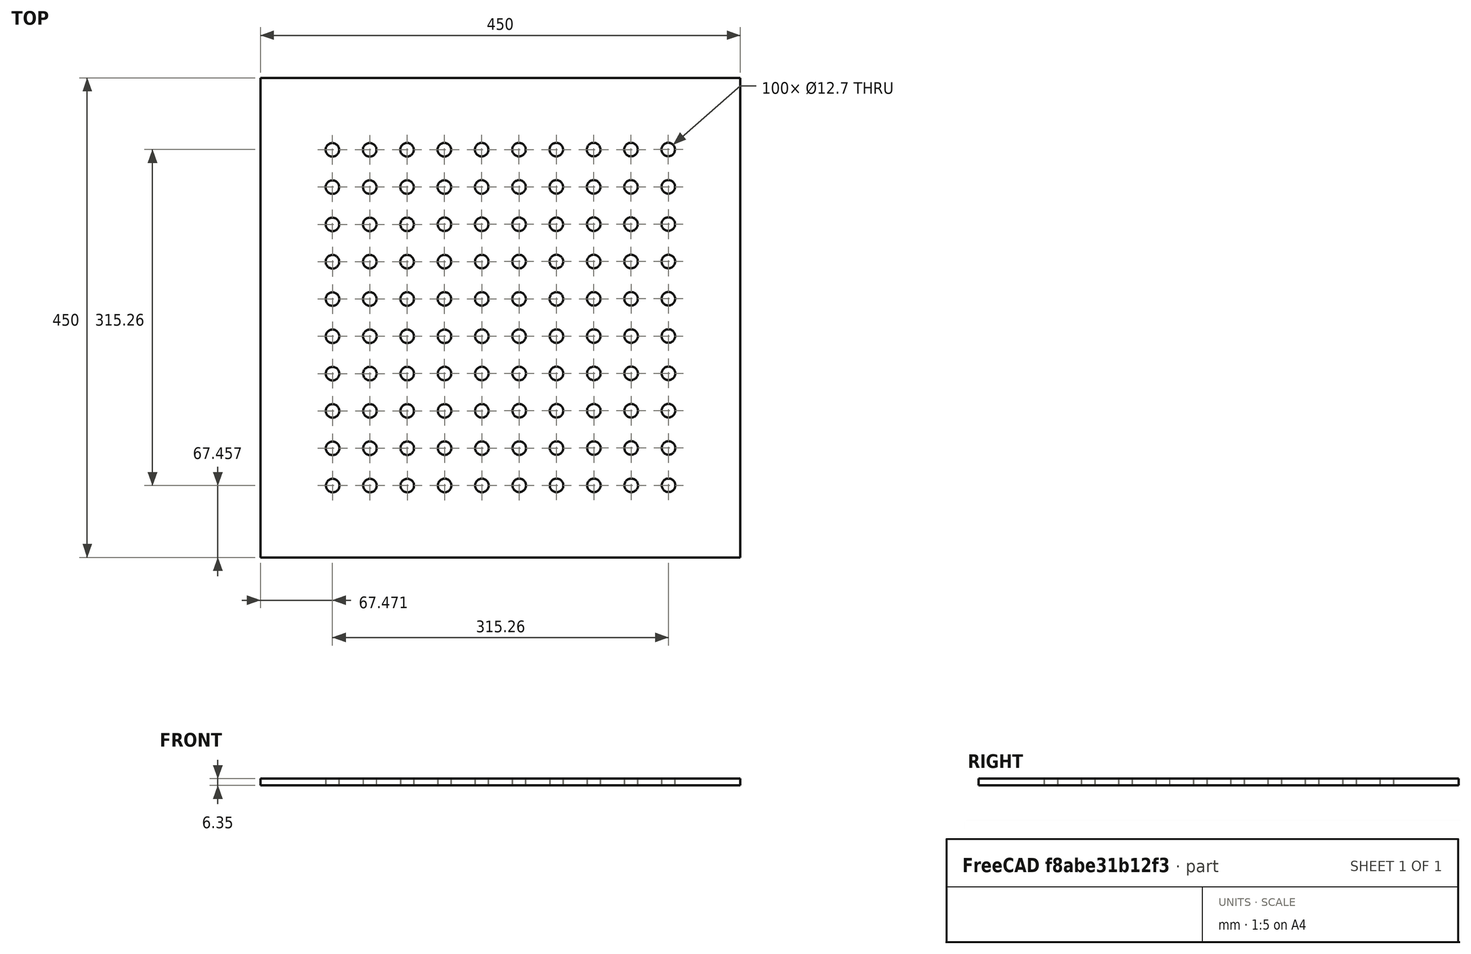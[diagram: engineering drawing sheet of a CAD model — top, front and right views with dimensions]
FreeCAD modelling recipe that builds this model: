
FCSTD DOCUMENT  (FreeCAD 0.16RUnknown)
Label: Tapa Perforada
License: All rights reserved
LicenseURL: http://berserk.design
objects: Sketcher::SketchObject×1, PartDesign::Pad×1
note: 3 computed .brp shape members not serialized (recipe doc carries the construction recipe); baked Part::Feature solids carry a one-line shape summary decoded from their .brp

FEATURE [Sketcher::SketchObject] Sketch
  sketch-geometry (207):
    g0: LineSegment StartX=0 StartY=0 StartZ=0 EndX=450 EndY=0 EndZ=0
    g1: LineSegment StartX=450 StartY=0 StartZ=0 EndX=450 EndY=450 EndZ=0
    g2: LineSegment StartX=450 StartY=450 StartZ=0 EndX=0 EndY=450 EndZ=0
    g3: LineSegment StartX=0 StartY=450 StartZ=0 EndX=0 EndY=0 EndZ=0
    g4: Circle CenterX=67.4711 CenterY=382.457 CenterZ=0 NormalX=0 NormalY=0 NormalZ=1 Radius=6.35
    g5: Circle CenterX=102.471 CenterY=382.485 CenterZ=0 NormalX=0 NormalY=0 NormalZ=1 Radius=6.35
    g6: LineSegment [constr] StartX=67.4711 StartY=382.457 StartZ=0 EndX=102.471 EndY=382.485 EndZ=0
    g7: Circle CenterX=137.471 CenterY=382.514 CenterZ=0 NormalX=0 NormalY=0 NormalZ=1 Radius=6.35
    g8: LineSegment [constr] StartX=102.471 StartY=382.485 StartZ=0 EndX=137.471 EndY=382.514 EndZ=0
    g9: Circle CenterX=172.471 CenterY=382.543 CenterZ=0 NormalX=0 NormalY=0 NormalZ=1 Radius=6.35
    g10: LineSegment [constr] StartX=137.471 StartY=382.514 StartZ=0 EndX=172.471 EndY=382.543 EndZ=0
    g11: Circle CenterX=207.471 CenterY=382.572 CenterZ=0 NormalX=0 NormalY=0 NormalZ=1 Radius=6.35
    g12: LineSegment [constr] StartX=172.471 StartY=382.543 StartZ=0 EndX=207.471 EndY=382.572 EndZ=0
    g13: Circle CenterX=242.471 CenterY=382.601 CenterZ=0 NormalX=0 NormalY=0 NormalZ=1 Radius=6.35
    g14: LineSegment [constr] StartX=207.471 StartY=382.572 StartZ=0 EndX=242.471 EndY=382.601 EndZ=0
    g15: Circle CenterX=277.471 CenterY=382.63 CenterZ=0 NormalX=0 NormalY=0 NormalZ=1 Radius=6.35
    g16: LineSegment [constr] StartX=242.471 StartY=382.601 StartZ=0 EndX=277.471 EndY=382.63 EndZ=0
    g17: Circle CenterX=312.471 CenterY=382.659 CenterZ=0 NormalX=0 NormalY=0 NormalZ=1 Radius=6.35
    g18: LineSegment [constr] StartX=277.471 StartY=382.63 StartZ=0 EndX=312.471 EndY=382.659 EndZ=0
    g19: Circle CenterX=347.471 CenterY=382.688 CenterZ=0 NormalX=0 NormalY=0 NormalZ=1 Radius=6.35
    g20: LineSegment [constr] StartX=312.471 StartY=382.659 StartZ=0 EndX=347.471 EndY=382.688 EndZ=0
    g21: Circle CenterX=382.471 CenterY=382.717 CenterZ=0 NormalX=0 NormalY=0 NormalZ=1 Radius=6.35
    g22: LineSegment [constr] StartX=347.471 StartY=382.688 StartZ=0 EndX=382.471 EndY=382.717 EndZ=0
    g23: Circle CenterX=67.5001 CenterY=347.457 CenterZ=0 NormalX=0 NormalY=0 NormalZ=1 Radius=6.35
    g24: LineSegment [constr] StartX=67.4711 StartY=382.457 StartZ=0 EndX=67.5001 EndY=347.457 EndZ=0
    g25: Circle CenterX=102.5 CenterY=347.485 CenterZ=0 NormalX=0 NormalY=0 NormalZ=1 Radius=6.35
    g26: LineSegment [constr] StartX=67.5001 StartY=347.457 StartZ=0 EndX=102.5 EndY=347.485 EndZ=0
    g27: Circle CenterX=137.5 CenterY=347.514 CenterZ=0 NormalX=0 NormalY=0 NormalZ=1 Radius=6.35
    g28: LineSegment [constr] StartX=102.5 StartY=347.485 StartZ=0 EndX=137.5 EndY=347.514 EndZ=0
    g29: Circle CenterX=172.5 CenterY=347.543 CenterZ=0 NormalX=0 NormalY=0 NormalZ=1 Radius=6.35
    g30: LineSegment [constr] StartX=137.5 StartY=347.514 StartZ=0 EndX=172.5 EndY=347.543 EndZ=0
    g31: Circle CenterX=207.5 CenterY=347.572 CenterZ=0 NormalX=0 NormalY=0 NormalZ=1 Radius=6.35
    g32: LineSegment [constr] StartX=172.5 StartY=347.543 StartZ=0 EndX=207.5 EndY=347.572 EndZ=0
    g33: Circle CenterX=242.5 CenterY=347.601 CenterZ=0 NormalX=0 NormalY=0 NormalZ=1 Radius=6.35
    g34: LineSegment [constr] StartX=207.5 StartY=347.572 StartZ=0 EndX=242.5 EndY=347.601 EndZ=0
    g35: Circle CenterX=277.5 CenterY=347.63 CenterZ=0 NormalX=0 NormalY=0 NormalZ=1 Radius=6.35
    g36: LineSegment [constr] StartX=242.5 StartY=347.601 StartZ=0 EndX=277.5 EndY=347.63 EndZ=0
    g37: Circle CenterX=312.5 CenterY=347.659 CenterZ=0 NormalX=0 NormalY=0 NormalZ=1 Radius=6.35
    g38: LineSegment [constr] StartX=277.5 StartY=347.63 StartZ=0 EndX=312.5 EndY=347.659 EndZ=0
    g39: Circle CenterX=347.5 CenterY=347.688 CenterZ=0 NormalX=0 NormalY=0 NormalZ=1 Radius=6.35
    g40: LineSegment [constr] StartX=312.5 StartY=347.659 StartZ=0 EndX=347.5 EndY=347.688 EndZ=0
    g41: Circle CenterX=382.5 CenterY=347.717 CenterZ=0 NormalX=0 NormalY=0 NormalZ=1 Radius=6.35
    g42: LineSegment [constr] StartX=347.5 StartY=347.688 StartZ=0 EndX=382.5 EndY=347.717 EndZ=0
    g43: Circle CenterX=67.529 CenterY=312.457 CenterZ=0 NormalX=0 NormalY=0 NormalZ=1 Radius=6.35
    g44: LineSegment [constr] StartX=67.5001 StartY=347.457 StartZ=0 EndX=67.529 EndY=312.457 EndZ=0
    g45: Circle CenterX=102.529 CenterY=312.486 CenterZ=0 NormalX=0 NormalY=0 NormalZ=1 Radius=6.35
    g46: LineSegment [constr] StartX=67.529 StartY=312.457 StartZ=0 EndX=102.529 EndY=312.486 EndZ=0
    g47: Circle CenterX=137.529 CenterY=312.514 CenterZ=0 NormalX=0 NormalY=0 NormalZ=1 Radius=6.35
    g48: LineSegment [constr] StartX=102.529 StartY=312.486 StartZ=0 EndX=137.529 EndY=312.514 EndZ=0
    g49: Circle CenterX=172.529 CenterY=312.543 CenterZ=0 NormalX=0 NormalY=0 NormalZ=1 Radius=6.35
    g50: LineSegment [constr] StartX=137.529 StartY=312.514 StartZ=0 EndX=172.529 EndY=312.543 EndZ=0
    g51: Circle CenterX=207.529 CenterY=312.572 CenterZ=0 NormalX=0 NormalY=0 NormalZ=1 Radius=6.35
    g52: LineSegment [constr] StartX=172.529 StartY=312.543 StartZ=0 EndX=207.529 EndY=312.572 EndZ=0
    g53: Circle CenterX=242.529 CenterY=312.601 CenterZ=0 NormalX=0 NormalY=0 NormalZ=1 Radius=6.35
    g54: LineSegment [constr] StartX=207.529 StartY=312.572 StartZ=0 EndX=242.529 EndY=312.601 EndZ=0
    g55: Circle CenterX=277.529 CenterY=312.63 CenterZ=0 NormalX=0 NormalY=0 NormalZ=1 Radius=6.35
    g56: LineSegment [constr] StartX=242.529 StartY=312.601 StartZ=0 EndX=277.529 EndY=312.63 EndZ=0
    g57: Circle CenterX=312.529 CenterY=312.659 CenterZ=0 NormalX=0 NormalY=0 NormalZ=1 Radius=6.35
    g58: LineSegment [constr] StartX=277.529 StartY=312.63 StartZ=0 EndX=312.529 EndY=312.659 EndZ=0
    g59: Circle CenterX=347.529 CenterY=312.688 CenterZ=0 NormalX=0 NormalY=0 NormalZ=1 Radius=6.35
    g60: LineSegment [constr] StartX=312.529 StartY=312.659 StartZ=0 EndX=347.529 EndY=312.688 EndZ=0
    g61: Circle CenterX=382.529 CenterY=312.717 CenterZ=0 NormalX=0 NormalY=0 NormalZ=1 Radius=6.35
    g62: LineSegment [constr] StartX=347.529 StartY=312.688 StartZ=0 EndX=382.529 EndY=312.717 EndZ=0
    g63: Circle CenterX=67.5579 CenterY=277.457 CenterZ=0 NormalX=0 NormalY=0 NormalZ=1 Radius=6.35
    g64: LineSegment [constr] StartX=67.529 StartY=312.457 StartZ=0 EndX=67.5579 EndY=277.457 EndZ=0
    g65: Circle CenterX=102.558 CenterY=277.486 CenterZ=0 NormalX=0 NormalY=0 NormalZ=1 Radius=6.35
    g66: LineSegment [constr] StartX=67.5579 StartY=277.457 StartZ=0 EndX=102.558 EndY=277.486 EndZ=0
    g67: Circle CenterX=137.558 CenterY=277.514 CenterZ=0 NormalX=0 NormalY=0 NormalZ=1 Radius=6.35
    g68: LineSegment [constr] StartX=102.558 StartY=277.486 StartZ=0 EndX=137.558 EndY=277.514 EndZ=0
    g69: Circle CenterX=172.558 CenterY=277.543 CenterZ=0 NormalX=0 NormalY=0 NormalZ=1 Radius=6.35
    g70: LineSegment [constr] StartX=137.558 StartY=277.514 StartZ=0 EndX=172.558 EndY=277.543 EndZ=0
    g71: Circle CenterX=207.558 CenterY=277.572 CenterZ=0 NormalX=0 NormalY=0 NormalZ=1 Radius=6.35
    g72: LineSegment [constr] StartX=172.558 StartY=277.543 StartZ=0 EndX=207.558 EndY=277.572 EndZ=0
    g73: Circle CenterX=242.558 CenterY=277.601 CenterZ=0 NormalX=0 NormalY=0 NormalZ=1 Radius=6.35
    g74: LineSegment [constr] StartX=207.558 StartY=277.572 StartZ=0 EndX=242.558 EndY=277.601 EndZ=0
    g75: Circle CenterX=277.558 CenterY=277.63 CenterZ=0 NormalX=0 NormalY=0 NormalZ=1 Radius=6.35
    g76: LineSegment [constr] StartX=242.558 StartY=277.601 StartZ=0 EndX=277.558 EndY=277.63 EndZ=0
    g77: Circle CenterX=312.558 CenterY=277.659 CenterZ=0 NormalX=0 NormalY=0 NormalZ=1 Radius=6.35
    g78: LineSegment [constr] StartX=277.558 StartY=277.63 StartZ=0 EndX=312.558 EndY=277.659 EndZ=0
    g79: Circle CenterX=347.558 CenterY=277.688 CenterZ=0 NormalX=0 NormalY=0 NormalZ=1 Radius=6.35
    g80: LineSegment [constr] StartX=312.558 StartY=277.659 StartZ=0 EndX=347.558 EndY=277.688 EndZ=0
    g81: Circle CenterX=382.558 CenterY=277.717 CenterZ=0 NormalX=0 NormalY=0 NormalZ=1 Radius=6.35
    g82: LineSegment [constr] StartX=347.558 StartY=277.688 StartZ=0 EndX=382.558 EndY=277.717 EndZ=0
    g83: Circle CenterX=67.5868 CenterY=242.457 CenterZ=0 NormalX=0 NormalY=0 NormalZ=1 Radius=6.35
    g84: LineSegment [constr] StartX=67.5579 StartY=277.457 StartZ=0 EndX=67.5868 EndY=242.457 EndZ=0
    g85: Circle CenterX=102.587 CenterY=242.486 CenterZ=0 NormalX=0 NormalY=0 NormalZ=1 Radius=6.35
    g86: LineSegment [constr] StartX=67.5868 StartY=242.457 StartZ=0 EndX=102.587 EndY=242.486 EndZ=0
    g87: Circle CenterX=137.587 CenterY=242.514 CenterZ=0 NormalX=0 NormalY=0 NormalZ=1 Radius=6.35
    g88: LineSegment [constr] StartX=102.587 StartY=242.486 StartZ=0 EndX=137.587 EndY=242.514 EndZ=0
    g89: Circle CenterX=172.587 CenterY=242.543 CenterZ=0 NormalX=0 NormalY=0 NormalZ=1 Radius=6.35
    g90: LineSegment [constr] StartX=137.587 StartY=242.514 StartZ=0 EndX=172.587 EndY=242.543 EndZ=0
    g91: Circle CenterX=207.587 CenterY=242.572 CenterZ=0 NormalX=0 NormalY=0 NormalZ=1 Radius=6.35
    g92: LineSegment [constr] StartX=172.587 StartY=242.543 StartZ=0 EndX=207.587 EndY=242.572 EndZ=0
    g93: Circle CenterX=242.587 CenterY=242.601 CenterZ=0 NormalX=0 NormalY=0 NormalZ=1 Radius=6.35
    g94: LineSegment [constr] StartX=207.587 StartY=242.572 StartZ=0 EndX=242.587 EndY=242.601 EndZ=0
    g95: Circle CenterX=277.587 CenterY=242.63 CenterZ=0 NormalX=0 NormalY=0 NormalZ=1 Radius=6.35
    g96: LineSegment [constr] StartX=242.587 StartY=242.601 StartZ=0 EndX=277.587 EndY=242.63 EndZ=0
    g97: Circle CenterX=312.587 CenterY=242.659 CenterZ=0 NormalX=0 NormalY=0 NormalZ=1 Radius=6.35
    g98: LineSegment [constr] StartX=277.587 StartY=242.63 StartZ=0 EndX=312.587 EndY=242.659 EndZ=0
    g99: Circle CenterX=347.587 CenterY=242.688 CenterZ=0 NormalX=0 NormalY=0 NormalZ=1 Radius=6.35
    g100: LineSegment [constr] StartX=312.587 StartY=242.659 StartZ=0 EndX=347.587 EndY=242.688 EndZ=0
    g101: Circle CenterX=382.587 CenterY=242.717 CenterZ=0 NormalX=0 NormalY=0 NormalZ=1 Radius=6.35
    g102: LineSegment [constr] StartX=347.587 StartY=242.688 StartZ=0 EndX=382.587 EndY=242.717 EndZ=0
    g103: Circle CenterX=67.6157 CenterY=207.457 CenterZ=0 NormalX=0 NormalY=0 NormalZ=1 Radius=6.35
    g104: LineSegment [constr] StartX=67.5868 StartY=242.457 StartZ=0 EndX=67.6157 EndY=207.457 EndZ=0
    g105: Circle CenterX=102.616 CenterY=207.486 CenterZ=0 NormalX=0 NormalY=0 NormalZ=1 Radius=6.35
    g106: LineSegment [constr] StartX=67.6157 StartY=207.457 StartZ=0 EndX=102.616 EndY=207.486 EndZ=0
    g107: Circle CenterX=137.616 CenterY=207.514 CenterZ=0 NormalX=0 NormalY=0 NormalZ=1 Radius=6.35
    g108: LineSegment [constr] StartX=102.616 StartY=207.486 StartZ=0 EndX=137.616 EndY=207.514 EndZ=0
    g109: Circle CenterX=172.616 CenterY=207.543 CenterZ=0 NormalX=0 NormalY=0 NormalZ=1 Radius=6.35
    g110: LineSegment [constr] StartX=137.616 StartY=207.514 StartZ=0 EndX=172.616 EndY=207.543 EndZ=0
    g111: Circle CenterX=207.616 CenterY=207.572 CenterZ=0 NormalX=0 NormalY=0 NormalZ=1 Radius=6.35
    g112: LineSegment [constr] StartX=172.616 StartY=207.543 StartZ=0 EndX=207.616 EndY=207.572 EndZ=0
    g113: Circle CenterX=242.616 CenterY=207.601 CenterZ=0 NormalX=0 NormalY=0 NormalZ=1 Radius=6.35
    g114: LineSegment [constr] StartX=207.616 StartY=207.572 StartZ=0 EndX=242.616 EndY=207.601 EndZ=0
    g115: Circle CenterX=277.616 CenterY=207.63 CenterZ=0 NormalX=0 NormalY=0 NormalZ=1 Radius=6.35
    g116: LineSegment [constr] StartX=242.616 StartY=207.601 StartZ=0 EndX=277.616 EndY=207.63 EndZ=0
    g117: Circle CenterX=312.616 CenterY=207.659 CenterZ=0 NormalX=0 NormalY=0 NormalZ=1 Radius=6.35
    g118: LineSegment [constr] StartX=277.616 StartY=207.63 StartZ=0 EndX=312.616 EndY=207.659 EndZ=0
    g119: Circle CenterX=347.616 CenterY=207.688 CenterZ=0 NormalX=0 NormalY=0 NormalZ=1 Radius=6.35
    g120: LineSegment [constr] StartX=312.616 StartY=207.659 StartZ=0 EndX=347.616 EndY=207.688 EndZ=0
    g121: Circle CenterX=382.616 CenterY=207.717 CenterZ=0 NormalX=0 NormalY=0 NormalZ=1 Radius=6.35
    g122: LineSegment [constr] StartX=347.616 StartY=207.688 StartZ=0 EndX=382.616 EndY=207.717 EndZ=0
    g123: Circle CenterX=67.6447 CenterY=172.457 CenterZ=0 NormalX=0 NormalY=0 NormalZ=1 Radius=6.35
    g124: LineSegment [constr] StartX=67.6157 StartY=207.457 StartZ=0 EndX=67.6447 EndY=172.457 EndZ=0
    g125: Circle CenterX=102.645 CenterY=172.486 CenterZ=0 NormalX=0 NormalY=0 NormalZ=1 Radius=6.35
    g126: LineSegment [constr] StartX=67.6447 StartY=172.457 StartZ=0 EndX=102.645 EndY=172.486 EndZ=0
    g127: Circle CenterX=137.645 CenterY=172.514 CenterZ=0 NormalX=0 NormalY=0 NormalZ=1 Radius=6.35
    g128: LineSegment [constr] StartX=102.645 StartY=172.486 StartZ=0 EndX=137.645 EndY=172.514 EndZ=0
    g129: Circle CenterX=172.645 CenterY=172.543 CenterZ=0 NormalX=0 NormalY=0 NormalZ=1 Radius=6.35
    g130: LineSegment [constr] StartX=137.645 StartY=172.514 StartZ=0 EndX=172.645 EndY=172.543 EndZ=0
    g131: Circle CenterX=207.645 CenterY=172.572 CenterZ=0 NormalX=0 NormalY=0 NormalZ=1 Radius=6.35
    g132: LineSegment [constr] StartX=172.645 StartY=172.543 StartZ=0 EndX=207.645 EndY=172.572 EndZ=0
    g133: Circle CenterX=242.645 CenterY=172.601 CenterZ=0 NormalX=0 NormalY=0 NormalZ=1 Radius=6.35
    g134: LineSegment [constr] StartX=207.645 StartY=172.572 StartZ=0 EndX=242.645 EndY=172.601 EndZ=0
    g135: Circle CenterX=277.645 CenterY=172.63 CenterZ=0 NormalX=0 NormalY=0 NormalZ=1 Radius=6.35
    g136: LineSegment [constr] StartX=242.645 StartY=172.601 StartZ=0 EndX=277.645 EndY=172.63 EndZ=0
    g137: Circle CenterX=312.645 CenterY=172.659 CenterZ=0 NormalX=0 NormalY=0 NormalZ=1 Radius=6.35
    g138: LineSegment [constr] StartX=277.645 StartY=172.63 StartZ=0 EndX=312.645 EndY=172.659 EndZ=0
    g139: Circle CenterX=347.645 CenterY=172.688 CenterZ=0 NormalX=0 NormalY=0 NormalZ=1 Radius=6.35
    g140: LineSegment [constr] StartX=312.645 StartY=172.659 StartZ=0 EndX=347.645 EndY=172.688 EndZ=0
    g141: Circle CenterX=382.645 CenterY=172.717 CenterZ=0 NormalX=0 NormalY=0 NormalZ=1 Radius=6.35
    g142: LineSegment [constr] StartX=347.645 StartY=172.688 StartZ=0 EndX=382.645 EndY=172.717 EndZ=0
    g143: Circle CenterX=67.6736 CenterY=137.457 CenterZ=0 NormalX=0 NormalY=0 NormalZ=1 Radius=6.35
    g144: LineSegment [constr] StartX=67.6447 StartY=172.457 StartZ=0 EndX=67.6736 EndY=137.457 EndZ=0
    g145: Circle CenterX=102.674 CenterY=137.486 CenterZ=0 NormalX=0 NormalY=0 NormalZ=1 Radius=6.35
    g146: LineSegment [constr] StartX=67.6736 StartY=137.457 StartZ=0 EndX=102.674 EndY=137.486 EndZ=0
    g147: Circle CenterX=137.674 CenterY=137.514 CenterZ=0 NormalX=0 NormalY=0 NormalZ=1 Radius=6.35
    g148: LineSegment [constr] StartX=102.674 StartY=137.486 StartZ=0 EndX=137.674 EndY=137.514 EndZ=0
    g149: Circle CenterX=172.674 CenterY=137.543 CenterZ=0 NormalX=0 NormalY=0 NormalZ=1 Radius=6.35
    g150: LineSegment [constr] StartX=137.674 StartY=137.514 StartZ=0 EndX=172.674 EndY=137.543 EndZ=0
    g151: Circle CenterX=207.674 CenterY=137.572 CenterZ=0 NormalX=0 NormalY=0 NormalZ=1 Radius=6.35
    g152: LineSegment [constr] StartX=172.674 StartY=137.543 StartZ=0 EndX=207.674 EndY=137.572 EndZ=0
    g153: Circle CenterX=242.674 CenterY=137.601 CenterZ=0 NormalX=0 NormalY=0 NormalZ=1 Radius=6.35
    g154: LineSegment [constr] StartX=207.674 StartY=137.572 StartZ=0 EndX=242.674 EndY=137.601 EndZ=0
    g155: Circle CenterX=277.674 CenterY=137.63 CenterZ=0 NormalX=0 NormalY=0 NormalZ=1 Radius=6.35
    g156: LineSegment [constr] StartX=242.674 StartY=137.601 StartZ=0 EndX=277.674 EndY=137.63 EndZ=0
    g157: Circle CenterX=312.673 CenterY=137.659 CenterZ=0 NormalX=0 NormalY=0 NormalZ=1 Radius=6.35
    g158: LineSegment [constr] StartX=277.674 StartY=137.63 StartZ=0 EndX=312.673 EndY=137.659 EndZ=0
    g159: Circle CenterX=347.673 CenterY=137.688 CenterZ=0 NormalX=0 NormalY=0 NormalZ=1 Radius=6.35
    g160: LineSegment [constr] StartX=312.673 StartY=137.659 StartZ=0 EndX=347.673 EndY=137.688 EndZ=0
    g161: Circle CenterX=382.673 CenterY=137.717 CenterZ=0 NormalX=0 NormalY=0 NormalZ=1 Radius=6.35
    g162: LineSegment [constr] StartX=347.673 StartY=137.688 StartZ=0 EndX=382.673 EndY=137.717 EndZ=0
    g163: Circle CenterX=67.7025 CenterY=102.457 CenterZ=0 NormalX=0 NormalY=0 NormalZ=1 Radius=6.35
    g164: LineSegment [constr] StartX=67.6736 StartY=137.457 StartZ=0 EndX=67.7025 EndY=102.457 EndZ=0
    g165: Circle CenterX=102.702 CenterY=102.486 CenterZ=0 NormalX=0 NormalY=0 NormalZ=1 Radius=6.35
    g166: LineSegment [constr] StartX=67.7025 StartY=102.457 StartZ=0 EndX=102.702 EndY=102.486 EndZ=0
    g167: Circle CenterX=137.702 CenterY=102.515 CenterZ=0 NormalX=0 NormalY=0 NormalZ=1 Radius=6.35
    g168: LineSegment [constr] StartX=102.702 StartY=102.486 StartZ=0 EndX=137.702 EndY=102.515 EndZ=0
    g169: Circle CenterX=172.702 CenterY=102.543 CenterZ=0 NormalX=0 NormalY=0 NormalZ=1 Radius=6.35
    g170: LineSegment [constr] StartX=137.702 StartY=102.515 StartZ=0 EndX=172.702 EndY=102.543 EndZ=0
    g171: Circle CenterX=207.702 CenterY=102.572 CenterZ=0 NormalX=0 NormalY=0 NormalZ=1 Radius=6.35
    g172: LineSegment [constr] StartX=172.702 StartY=102.543 StartZ=0 EndX=207.702 EndY=102.572 EndZ=0
    g173: Circle CenterX=242.702 CenterY=102.601 CenterZ=0 NormalX=0 NormalY=0 NormalZ=1 Radius=6.35
    g174: LineSegment [constr] StartX=207.702 StartY=102.572 StartZ=0 EndX=242.702 EndY=102.601 EndZ=0
    g175: Circle CenterX=277.702 CenterY=102.63 CenterZ=0 NormalX=0 NormalY=0 NormalZ=1 Radius=6.35
    g176: LineSegment [constr] StartX=242.702 StartY=102.601 StartZ=0 EndX=277.702 EndY=102.63 EndZ=0
    g177: Circle CenterX=312.702 CenterY=102.659 CenterZ=0 NormalX=0 NormalY=0 NormalZ=1 Radius=6.35
    g178: LineSegment [constr] StartX=277.702 StartY=102.63 StartZ=0 EndX=312.702 EndY=102.659 EndZ=0
    g179: Circle CenterX=347.702 CenterY=102.688 CenterZ=0 NormalX=0 NormalY=0 NormalZ=1 Radius=6.35
    g180: LineSegment [constr] StartX=312.702 StartY=102.659 StartZ=0 EndX=347.702 EndY=102.688 EndZ=0
    g181: Circle CenterX=382.702 CenterY=102.717 CenterZ=0 NormalX=0 NormalY=0 NormalZ=1 Radius=6.35
    g182: LineSegment [constr] StartX=347.702 StartY=102.688 StartZ=0 EndX=382.702 EndY=102.717 EndZ=0
    g183: Circle CenterX=67.7314 CenterY=67.4567 CenterZ=0 NormalX=0 NormalY=0 NormalZ=1 Radius=6.35
    g184: LineSegment [constr] StartX=67.7025 StartY=102.457 StartZ=0 EndX=67.7314 EndY=67.4567 EndZ=0
    g185: Circle CenterX=102.731 CenterY=67.4856 CenterZ=0 NormalX=0 NormalY=0 NormalZ=1 Radius=6.35
    g186: LineSegment [constr] StartX=67.7314 StartY=67.4567 StartZ=0 EndX=102.731 EndY=67.4856 EndZ=0
    g187: Circle CenterX=137.731 CenterY=67.5145 CenterZ=0 NormalX=0 NormalY=0 NormalZ=1 Radius=6.35
    g188: LineSegment [constr] StartX=102.731 StartY=67.4856 StartZ=0 EndX=137.731 EndY=67.5145 EndZ=0
    g189: Circle CenterX=172.731 CenterY=67.5434 CenterZ=0 NormalX=0 NormalY=0 NormalZ=1 Radius=6.35
    g190: LineSegment [constr] StartX=137.731 StartY=67.5145 StartZ=0 EndX=172.731 EndY=67.5434 EndZ=0
    g191: Circle CenterX=207.731 CenterY=67.5724 CenterZ=0 NormalX=0 NormalY=0 NormalZ=1 Radius=6.35
    g192: LineSegment [constr] StartX=172.731 StartY=67.5434 StartZ=0 EndX=207.731 EndY=67.5724 EndZ=0
    g193: Circle CenterX=242.731 CenterY=67.6013 CenterZ=0 NormalX=0 NormalY=0 NormalZ=1 Radius=6.35
    g194: LineSegment [constr] StartX=207.731 StartY=67.5724 StartZ=0 EndX=242.731 EndY=67.6013 EndZ=0
    g195: Circle CenterX=277.731 CenterY=67.6302 CenterZ=0 NormalX=0 NormalY=0 NormalZ=1 Radius=6.35
    g196: LineSegment [constr] StartX=242.731 StartY=67.6013 StartZ=0 EndX=277.731 EndY=67.6302 EndZ=0
    g197: Circle CenterX=312.731 CenterY=67.6591 CenterZ=0 NormalX=0 NormalY=0 NormalZ=1 Radius=6.35
    g198: LineSegment [constr] StartX=277.731 StartY=67.6302 StartZ=0 EndX=312.731 EndY=67.6591 EndZ=0
    g199: Circle CenterX=347.731 CenterY=67.688 CenterZ=0 NormalX=0 NormalY=0 NormalZ=1 Radius=6.35
    g200: LineSegment [constr] StartX=312.731 StartY=67.6591 StartZ=0 EndX=347.731 EndY=67.688 EndZ=0
    g201: Circle CenterX=382.731 CenterY=67.717 CenterZ=0 NormalX=0 NormalY=0 NormalZ=1 Radius=6.35
    g202: LineSegment [constr] StartX=347.731 StartY=67.688 StartZ=0 EndX=382.731 EndY=67.717 EndZ=0
    g203: LineSegment [constr] StartX=0 StartY=347.457 StartZ=0 EndX=67.5001 EndY=347.457 EndZ=0
    g204: LineSegment [constr] StartX=382.5 StartY=347.717 StartZ=0 EndX=450 EndY=347.717 EndZ=0
    g205: LineSegment [constr] StartX=67.7314 StartY=67.4567 StartZ=0 EndX=67.7314 EndY=0 EndZ=0
    g206: LineSegment [constr] StartX=172.471 StartY=382.543 StartZ=0 EndX=172.471 EndY=450 EndZ=0
  constraints (521):
    c: Coincident(g0,g1)
    c: Coincident(g1,g2)
    c: Coincident(g2,g3)
    c: Coincident(g3,g0)
    c: Horizontal(g0)
    c: Horizontal(g2)
    c: Vertical(g1)
    c: Vertical(g3)
    c: Coincident(g0,g-1)
    c: DistanceX(g2,g2) = 450
    c: DistanceY(g3,g3) = 450
    c: Radius(g4) = 6.35
    c: Radius(g5) = 6.35
    c: Coincident(g4,g6)
    c: Coincident(g5,g6)
    c: Distance(g6) = 35
    c: Angle(g6) = 0.000826333
    c: Radius(g7) = 6.35
    c: Coincident(g5,g8)
    c: Coincident(g7,g8)
    c: Equal(g6,g8)
    c: Parallel(g8,g6)
    c: Radius(g9) = 6.35
    c: Coincident(g7,g10)
    c: Coincident(g9,g10)
    c: Equal(g6,g10)
    c: Parallel(g10,g6)
    c: Radius(g11) = 6.35
    c: Coincident(g9,g12)
    c: Coincident(g11,g12)
    c: Equal(g6,g12)
    c: Parallel(g12,g6)
    c: Radius(g13) = 6.35
    c: Coincident(g11,g14)
    c: Coincident(g13,g14)
    c: Equal(g6,g14)
    c: Parallel(g14,g6)
    c: Radius(g15) = 6.35
    c: Coincident(g13,g16)
    c: Coincident(g15,g16)
    c: Equal(g6,g16)
    c: Parallel(g16,g6)
    c: Radius(g17) = 6.35
    c: Coincident(g15,g18)
    c: Coincident(g17,g18)
    c: Equal(g6,g18)
    c: Parallel(g18,g6)
    c: Radius(g19) = 6.35
    c: Coincident(g17,g20)
    c: Coincident(g19,g20)
    c: Equal(g6,g20)
    c: Parallel(g20,g6)
    c: Radius(g21) = 6.35
    c: Coincident(g19,g22)
    c: Coincident(g21,g22)
    c: Equal(g6,g22)
    c: Parallel(g22,g6)
    c: Radius(g23) = 6.35
    c: Coincident(g4,g24)
    c: Coincident(g23,g24)
    c: Equal(g24,g6)
    c: Perpendicular(g24,g6)
    c: Radius(g25) = 6.35
    c: Coincident(g23,g26)
    c: Coincident(g25,g26)
    c: Equal(g6,g26)
    c: Parallel(g26,g6)
    c: Radius(g27) = 6.35
    c: Coincident(g25,g28)
    c: Coincident(g27,g28)
    c: Equal(g6,g28)
    c: Parallel(g28,g6)
    c: Radius(g29) = 6.35
    c: Coincident(g27,g30)
    c: Coincident(g29,g30)
    c: Equal(g6,g30)
    c: Parallel(g30,g6)
    c: Radius(g31) = 6.35
    c: Coincident(g29,g32)
    c: Coincident(g31,g32)
    c: Equal(g6,g32)
    c: Parallel(g32,g6)
    c: Radius(g33) = 6.35
    c: Coincident(g31,g34)
    c: Coincident(g33,g34)
    c: Equal(g6,g34)
    c: Parallel(g34,g6)
    c: Radius(g35) = 6.35
    c: Coincident(g33,g36)
    c: Coincident(g35,g36)
    c: Equal(g6,g36)
    c: Parallel(g36,g6)
    c: Radius(g37) = 6.35
    c: Coincident(g35,g38)
    c: Coincident(g37,g38)
    c: Equal(g6,g38)
    c: Parallel(g38,g6)
    c: Radius(g39) = 6.35
    c: Coincident(g37,g40)
    c: Coincident(g39,g40)
    c: Equal(g6,g40)
    c: Parallel(g40,g6)
    c: Radius(g41) = 6.35
    c: Coincident(g39,g42)
    c: Coincident(g41,g42)
    c: Equal(g6,g42)
    c: Parallel(g42,g6)
    c: Radius(g43) = 6.35
    c: Coincident(g23,g44)
    c: Coincident(g43,g44)
    c: Equal(g24,g44)
    c: Perpendicular(g44,g6)
    c: Radius(g45) = 6.35
    c: Coincident(g43,g46)
    c: Coincident(g45,g46)
    c: Equal(g6,g46)
    c: Parallel(g46,g6)
    c: Radius(g47) = 6.35
    c: Coincident(g45,g48)
    c: Coincident(g47,g48)
    c: Equal(g6,g48)
    c: Parallel(g48,g6)
    c: Radius(g49) = 6.35
    c: Coincident(g47,g50)
    c: Coincident(g49,g50)
    c: Equal(g6,g50)
    c: Parallel(g50,g6)
    c: Radius(g51) = 6.35
    c: Coincident(g49,g52)
    c: Coincident(g51,g52)
    c: Equal(g6,g52)
    c: Parallel(g52,g6)
    c: Radius(g53) = 6.35
    c: Coincident(g51,g54)
    c: Coincident(g53,g54)
    c: Equal(g6,g54)
    c: Parallel(g54,g6)
    c: Radius(g55) = 6.35
    c: Coincident(g53,g56)
    c: Coincident(g55,g56)
    c: Equal(g6,g56)
    c: Parallel(g56,g6)
    c: Radius(g57) = 6.35
    c: Coincident(g55,g58)
    c: Coincident(g57,g58)
    c: Equal(g6,g58)
    c: Parallel(g58,g6)
    c: Radius(g59) = 6.35
    c: Coincident(g57,g60)
    c: Coincident(g59,g60)
    c: Equal(g6,g60)
    c: Parallel(g60,g6)
    c: Radius(g61) = 6.35
    c: Coincident(g59,g62)
    c: Coincident(g61,g62)
    c: Equal(g6,g62)
    c: Parallel(g62,g6)
    c: Radius(g63) = 6.35
    c: Coincident(g43,g64)
    c: Coincident(g63,g64)
    c: Equal(g24,g64)
    c: Perpendicular(g64,g6)
    c: Radius(g65) = 6.35
    c: Coincident(g63,g66)
    c: Coincident(g65,g66)
    c: Equal(g6,g66)
    c: Parallel(g66,g6)
    c: Radius(g67) = 6.35
    c: Coincident(g65,g68)
    c: Coincident(g67,g68)
    c: Equal(g6,g68)
    c: Parallel(g68,g6)
    c: Radius(g69) = 6.35
    c: Coincident(g67,g70)
    c: Coincident(g69,g70)
    c: Equal(g6,g70)
    c: Parallel(g70,g6)
    c: Radius(g71) = 6.35
    c: Coincident(g69,g72)
    c: Coincident(g71,g72)
    c: Equal(g6,g72)
    c: Parallel(g72,g6)
    c: Radius(g73) = 6.35
    c: Coincident(g71,g74)
    c: Coincident(g73,g74)
    c: Equal(g6,g74)
    c: Parallel(g74,g6)
    c: Radius(g75) = 6.35
    c: Coincident(g73,g76)
    c: Coincident(g75,g76)
    c: Equal(g6,g76)
    c: Parallel(g76,g6)
    c: Radius(g77) = 6.35
    c: Coincident(g75,g78)
    c: Coincident(g77,g78)
    c: Equal(g6,g78)
    c: Parallel(g78,g6)
    c: Radius(g79) = 6.35
    c: Coincident(g77,g80)
    c: Coincident(g79,g80)
    c: Equal(g6,g80)
    c: Parallel(g80,g6)
    c: Radius(g81) = 6.35
    c: Coincident(g79,g82)
    c: Coincident(g81,g82)
    c: Equal(g6,g82)
    c: Parallel(g82,g6)
    c: Radius(g83) = 6.35
    c: Coincident(g63,g84)
    c: Coincident(g83,g84)
    c: Equal(g24,g84)
    c: Perpendicular(g84,g6)
    c: Radius(g85) = 6.35
    c: Coincident(g83,g86)
    c: Coincident(g85,g86)
    c: Equal(g6,g86)
    c: Parallel(g86,g6)
    c: Radius(g87) = 6.35
    c: Coincident(g85,g88)
    c: Coincident(g87,g88)
    c: Equal(g6,g88)
    c: Parallel(g88,g6)
    c: Radius(g89) = 6.35
    c: Coincident(g87,g90)
    c: Coincident(g89,g90)
    c: Equal(g6,g90)
    c: Parallel(g90,g6)
    c: Radius(g91) = 6.35
    c: Coincident(g89,g92)
    c: Coincident(g91,g92)
    c: Equal(g6,g92)
    c: Parallel(g92,g6)
    c: Radius(g93) = 6.35
    c: Coincident(g91,g94)
    c: Coincident(g93,g94)
    c: Equal(g6,g94)
    c: Parallel(g94,g6)
    c: Radius(g95) = 6.35
    c: Coincident(g93,g96)
    c: Coincident(g95,g96)
    c: Equal(g6,g96)
    c: Parallel(g96,g6)
    c: Radius(g97) = 6.35
    c: Coincident(g95,g98)
    c: Coincident(g97,g98)
    c: Equal(g6,g98)
    c: Parallel(g98,g6)
    c: Radius(g99) = 6.35
    c: Coincident(g97,g100)
    c: Coincident(g99,g100)
    c: Equal(g6,g100)
    c: Parallel(g100,g6)
    c: Radius(g101) = 6.35
    c: Coincident(g99,g102)
    c: Coincident(g101,g102)
    c: Equal(g6,g102)
    c: Parallel(g102,g6)
    c: Radius(g103) = 6.35
    c: Coincident(g83,g104)
    c: Coincident(g103,g104)
    c: Equal(g24,g104)
    c: Perpendicular(g104,g6)
    c: Radius(g105) = 6.35
    c: Coincident(g103,g106)
    c: Coincident(g105,g106)
    c: Equal(g6,g106)
    c: Parallel(g106,g6)
    c: Radius(g107) = 6.35
    c: Coincident(g105,g108)
    c: Coincident(g107,g108)
    c: Equal(g6,g108)
    c: Parallel(g108,g6)
    c: Radius(g109) = 6.35
    c: Coincident(g107,g110)
    c: Coincident(g109,g110)
    c: Equal(g6,g110)
    c: Parallel(g110,g6)
    c: Radius(g111) = 6.35
    c: Coincident(g109,g112)
    c: Coincident(g111,g112)
    c: Equal(g6,g112)
    c: Parallel(g112,g6)
    c: Radius(g113) = 6.35
    c: Coincident(g111,g114)
    c: Coincident(g113,g114)
    c: Equal(g6,g114)
    c: Parallel(g114,g6)
    c: Radius(g115) = 6.35
    c: Coincident(g113,g116)
    c: Coincident(g115,g116)
    c: Equal(g6,g116)
    c: Parallel(g116,g6)
    c: Radius(g117) = 6.35
    c: Coincident(g115,g118)
    c: Coincident(g117,g118)
    c: Equal(g6,g118)
    c: Parallel(g118,g6)
    c: Radius(g119) = 6.35
    c: Coincident(g117,g120)
    c: Coincident(g119,g120)
    c: Equal(g6,g120)
    c: Parallel(g120,g6)
    c: Radius(g121) = 6.35
    c: Coincident(g119,g122)
    c: Coincident(g121,g122)
    c: Equal(g6,g122)
    c: Parallel(g122,g6)
    c: Radius(g123) = 6.35
    c: Coincident(g103,g124)
    c: Coincident(g123,g124)
    c: Equal(g24,g124)
    c: Perpendicular(g124,g6)
    c: Radius(g125) = 6.35
    c: Coincident(g123,g126)
    c: Coincident(g125,g126)
    c: Equal(g6,g126)
    c: Parallel(g126,g6)
    c: Radius(g127) = 6.35
    c: Coincident(g125,g128)
    c: Coincident(g127,g128)
    c: Equal(g6,g128)
    c: Parallel(g128,g6)
    c: Radius(g129) = 6.35
    c: Coincident(g127,g130)
    c: Coincident(g129,g130)
    c: Equal(g6,g130)
    c: Parallel(g130,g6)
    c: Radius(g131) = 6.35
    c: Coincident(g129,g132)
    c: Coincident(g131,g132)
    c: Equal(g6,g132)
    c: Parallel(g132,g6)
    c: Radius(g133) = 6.35
    c: Coincident(g131,g134)
    c: Coincident(g133,g134)
    c: Equal(g6,g134)
    c: Parallel(g134,g6)
    c: Radius(g135) = 6.35
    c: Coincident(g133,g136)
    c: Coincident(g135,g136)
    c: Equal(g6,g136)
    c: Parallel(g136,g6)
    c: Radius(g137) = 6.35
    c: Coincident(g135,g138)
    c: Coincident(g137,g138)
    c: Equal(g6,g138)
    c: Parallel(g138,g6)
    c: Radius(g139) = 6.35
    c: Coincident(g137,g140)
    c: Coincident(g139,g140)
    c: Equal(g6,g140)
    c: Parallel(g140,g6)
    c: Radius(g141) = 6.35
    c: Coincident(g139,g142)
    c: Coincident(g141,g142)
    c: Equal(g6,g142)
    c: Parallel(g142,g6)
    c: Radius(g143) = 6.35
    c: Coincident(g123,g144)
    c: Coincident(g143,g144)
    c: Equal(g24,g144)
    c: Perpendicular(g144,g6)
    c: Radius(g145) = 6.35
    c: Coincident(g143,g146)
    c: Coincident(g145,g146)
    c: Equal(g6,g146)
    c: Parallel(g146,g6)
    c: Radius(g147) = 6.35
    c: Coincident(g145,g148)
    c: Coincident(g147,g148)
    c: Equal(g6,g148)
    c: Parallel(g148,g6)
    c: Radius(g149) = 6.35
    c: Coincident(g147,g150)
    c: Coincident(g149,g150)
    c: Equal(g6,g150)
    c: Parallel(g150,g6)
    c: Radius(g151) = 6.35
    c: Coincident(g149,g152)
    c: Coincident(g151,g152)
    c: Equal(g6,g152)
    c: Parallel(g152,g6)
    c: Radius(g153) = 6.35
    c: Coincident(g151,g154)
    c: Coincident(g153,g154)
    c: Equal(g6,g154)
    c: Parallel(g154,g6)
    c: Radius(g155) = 6.35
    c: Coincident(g153,g156)
    c: Coincident(g155,g156)
    c: Equal(g6,g156)
    c: Parallel(g156,g6)
    c: Radius(g157) = 6.35
    c: Coincident(g155,g158)
    c: Coincident(g157,g158)
    c: Equal(g6,g158)
    c: Parallel(g158,g6)
    c: Radius(g159) = 6.35
    c: Coincident(g157,g160)
    c: Coincident(g159,g160)
    c: Equal(g6,g160)
    c: Parallel(g160,g6)
    c: Radius(g161) = 6.35
    c: Coincident(g159,g162)
    c: Coincident(g161,g162)
    c: Equal(g6,g162)
    c: Parallel(g162,g6)
    c: Radius(g163) = 6.35
    c: Coincident(g143,g164)
    c: Coincident(g163,g164)
    c: Equal(g24,g164)
    c: Perpendicular(g164,g6)
    c: Radius(g165) = 6.35
    c: Coincident(g163,g166)
    c: Coincident(g165,g166)
    c: Equal(g6,g166)
    c: Parallel(g166,g6)
    c: Radius(g167) = 6.35
    c: Coincident(g165,g168)
    c: Coincident(g167,g168)
    c: Equal(g6,g168)
    c: Parallel(g168,g6)
    c: Radius(g169) = 6.35
    c: Coincident(g167,g170)
    c: Coincident(g169,g170)
    c: Equal(g6,g170)
    c: Parallel(g170,g6)
    c: Radius(g171) = 6.35
    c: Coincident(g169,g172)
    c: Coincident(g171,g172)
    c: Equal(g6,g172)
    c: Parallel(g172,g6)
    c: Radius(g173) = 6.35
    c: Coincident(g171,g174)
    c: Coincident(g173,g174)
    c: Equal(g6,g174)
    c: Parallel(g174,g6)
    c: Radius(g175) = 6.35
    c: Coincident(g173,g176)
    c: Coincident(g175,g176)
    c: Equal(g6,g176)
    c: Parallel(g176,g6)
    c: Radius(g177) = 6.35
    c: Coincident(g175,g178)
    c: Coincident(g177,g178)
    c: Equal(g6,g178)
    c: Parallel(g178,g6)
    c: Radius(g179) = 6.35
    c: Coincident(g177,g180)
    c: Coincident(g179,g180)
    c: Equal(g6,g180)
    c: Parallel(g180,g6)
    c: Radius(g181) = 6.35
    c: Coincident(g179,g182)
    c: Coincident(g181,g182)
    c: Equal(g6,g182)
    c: Parallel(g182,g6)
    c: Radius(g183) = 6.35
    c: Coincident(g163,g184)
    c: Coincident(g183,g184)
    c: Equal(g24,g184)
    c: Perpendicular(g184,g6)
    c: Radius(g185) = 6.35
    c: Coincident(g183,g186)
    c: Coincident(g185,g186)
    c: Equal(g6,g186)
    c: Parallel(g186,g6)
    c: Radius(g187) = 6.35
    c: Coincident(g185,g188)
    c: Coincident(g187,g188)
    c: Equal(g6,g188)
    c: Parallel(g188,g6)
    c: Radius(g189) = 6.35
    c: Coincident(g187,g190)
    c: Coincident(g189,g190)
    c: Equal(g6,g190)
    c: Parallel(g190,g6)
    c: Radius(g191) = 6.35
    c: Coincident(g189,g192)
    c: Coincident(g191,g192)
    c: Equal(g6,g192)
    c: Parallel(g192,g6)
    c: Radius(g193) = 6.35
    c: Coincident(g191,g194)
    c: Coincident(g193,g194)
    c: Equal(g6,g194)
    c: Parallel(g194,g6)
    c: Radius(g195) = 6.35
    c: Coincident(g193,g196)
    c: Coincident(g195,g196)
    c: Equal(g6,g196)
    c: Parallel(g196,g6)
    c: Radius(g197) = 6.35
    c: Coincident(g195,g198)
    c: Coincident(g197,g198)
    c: Equal(g6,g198)
    c: Parallel(g198,g6)
    c: Radius(g199) = 6.35
    c: Coincident(g197,g200)
    c: Coincident(g199,g200)
    c: Equal(g6,g200)
    c: Parallel(g200,g6)
    c: Radius(g201) = 6.35
    c: Coincident(g199,g202)
    c: Coincident(g201,g202)
    c: Equal(g6,g202)
    c: Parallel(g202,g6)
    c: PointOnObject(g203,g3)
    c: Coincident(g203,g23)
    c: Horizontal(g203)
    c: Coincident(g204,g41)
    c: PointOnObject(g204,g1)
    c: Horizontal(g204)
    c: Equal(g203,g204)
    c: Coincident(g205,g183)
    c: PointOnObject(g205,g0)
    c: Vertical(g205)
    c: Coincident(g206,g9)
    c: PointOnObject(g206,g2)
    c: Vertical(g206)
    c: Equal(g206,g205)
FEATURE [PartDesign::Pad] Pad
  Length = 6.35
  Length2 = 100
  Sketch = -> Sketch
  Type = 0
